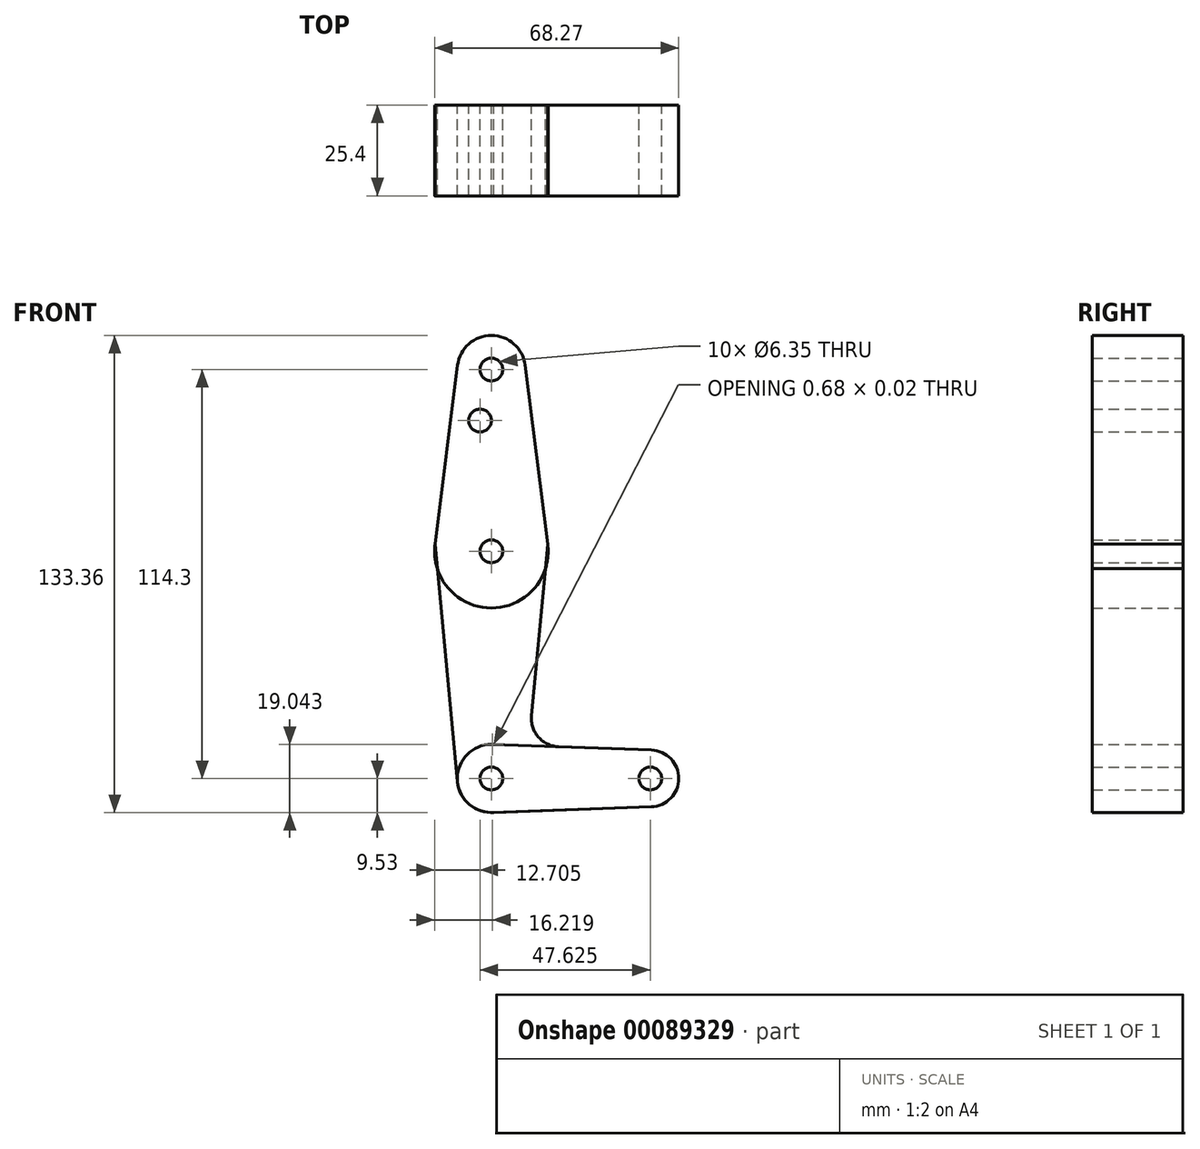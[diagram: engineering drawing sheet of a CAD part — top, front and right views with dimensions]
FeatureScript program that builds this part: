
annotation { "Feature Type Name" : "Feature", "Feature Type Description" : "" }
export const myFeature = defineFeature(function(context is Context, id is Id, definition is map)
    precondition{}
    {
        {
            var Q0;
            Q0=qCreatedBy(makeId("Front.planeOp"),FACE);
            var sketch = newSketch(context, id + "F0", { "sketchPlane" : qUnion([Q0])});
            skCircle(sketch, "E0", {"center": v(0, 114.3) * mm, "radius": 9.53 * mm});
            skCircle(sketch, "E1", {"center": v(0, 63.5) * mm, "radius": 15.88 * mm});
            skCircle(sketch, "E2", {"center": v(0, 0) * mm, "radius": 9.53 * mm});
            skCircle(sketch, "E3", {"center": v(44.45, 0) * mm, "radius": 7.94 * mm});
            skLineSegment(sketch, "E4", {"start": v(9.45, 115.5) * mm, "end": v(15.75, 65.48) * mm});
            skLineSegment(sketch, "E5", {"start": v(-9.45, 115.5) * mm, "end": v(-15.75, 65.48) * mm});
            skLineSegment(sketch, "E6", {"start": v(-15.75, 65.48) * mm, "end": v(-9.48, -0.9) * mm});
            skLineSegment(sketch, "E7", {"start": v(15.75, 65.48) * mm, "end": v(9.57, 0) * mm});
            skLineSegment(sketch, "E8", {"start": v(0, 9.53) * mm, "end": v(0.68, 9.5) * mm});
            skLineSegment(sketch, "E9", {"start": v(0, -9.53) * mm, "end": v(44.73, -7.93) * mm});
            skLineSegment(sketch, "E10", {"start": v(0.68, 9.5) * mm, "end": v(22.7, 8.72) * mm});
            skPoint(sketch, "E11.end.orphan", {"position": v(22.7, 8.72) * mm});
            skArc(sketch, "E12", {"start": v(11.22, 17.55) * mm, "mid": v(13.16, 11.55) * mm, "end": v(18.86, 8.85) * mm});
            skPoint(sketch, "E13.orphan", {"position": v(44.73, 7.93) * mm});
            skLineSegment(sketch, "E14", {"start": v(18.86, 8.85) * mm, "end": v(44.73, 7.93) * mm});
            skCircle(sketch, "E15", {"center": v(44.45, 0) * mm, "radius": 3.18 * mm});
            skCircle(sketch, "E16", {"center": v(0, 114.3) * mm, "radius": 3.18 * mm});
            skCircle(sketch, "E17", {"center": v(0, 63.5) * mm, "radius": 3.18 * mm});
            skCircle(sketch, "E18", {"center": v(0, 0) * mm, "radius": 3.18 * mm});
            skCircle(sketch, "E19", {"center": v(-3.18, 100.03) * mm, "radius": 3.18 * mm});
            skLineSegment(sketch, "E20", {"start": v(0, 114.3) * mm, "end": v(0, 63.5) * mm});
            skSolve(sketch);
        }
        {
            var Q0;
            {var subQ1=sQuery(id+"F0.wireOp",EDGE,"E5");Q0=makeQuery(id+"F0.imprint","IMPRINT",FACE,{"disambiguationData":[TD([[makeQuery(id+"F0.imprint","IMPRINT",EDGE,{"derivedFrom":subQ1}),1.0]])]});}
            var Q1;
            {var subQ0=sQuery(id+"F0.wireOp",EDGE,"E4");Q1=makeQuery(id+"F0.imprint","IMPRINT",FACE,{"disambiguationData":[TD([[makeQuery(id+"F0.imprint","IMPRINT",EDGE,{"derivedFrom":subQ0}),-1.0]])]});}
            var Q2;
            Q2=makeQuery(id+"F0.imprint","IMPRINT",FACE,{"disambiguationData":[TD([[makeQuery(id+"F0.imprint","IMPRINT",EDGE,{"derivedFrom":sQuery(id+"F0.wireOp",EDGE,"E16")}),-1.0]])]});
            var Q3;
            Q3=makeQuery(id+"F0.imprint","IMPRINT",FACE,{"disambiguationData":[TD([[makeQuery(id+"F0.imprint","IMPRINT",EDGE,{"derivedFrom":sQuery(id+"F0.wireOp",EDGE,"E17")}),-1.0]])]});
            var Q4;
            {var subQ4=sQuery(id+"F0.wireOp",EDGE,"E8");Q4=makeQuery(id+"F0.imprint","IMPRINT",FACE,{"disambiguationData":[TD([[makeQuery(id+"F0.imprint","IMPRINT",EDGE,{"derivedFrom":subQ4}),-1.0]])]});}
            var Q5;
            {var subQ4=sQuery(id+"F0.wireOp",EDGE,"E14");var subQ11=makeQuery(id+"F0.imprint","IMPRINT",VERTEX,{"derivedFrom":subQ4});Q5=makeQuery(id+"F0.imprint","IMPRINT",FACE,{"disambiguationData":[TD([[makeQuery(id+"F0.imprint","IMPRINT",EDGE,{"disambiguationData":[TD([[subQ11,-1.0]])],"derivedFrom":subQ4}),-1.0]])]});}
            var Q6;
            Q6=makeQuery(id+"F0.imprint","IMPRINT",FACE,{"disambiguationData":[TD([[makeQuery(id+"F0.imprint","IMPRINT",EDGE,{"derivedFrom":sQuery(id+"F0.wireOp",EDGE,"E15")}),-1.0]])]});
            extrude(context, id + "F1", {"entities" : qUnion([Q0, Q1, Q2, Q3, Q4, Q5, Q6]), "depth" : 25.4 * mm});
        }
        {
            var Q0;
            Q0 = qSketchRegion(id + "F0", true);
            extrude(context, id + "F2", {"entities" : qUnion([Q0]), "depth" : 25.4 * mm});
        }
    });
